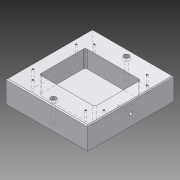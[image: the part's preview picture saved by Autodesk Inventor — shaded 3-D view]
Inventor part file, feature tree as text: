
AUTODESK INVENTOR PART (.ipt)
format: ipt  version: 2013 (Build 170138000, 138)  size: 171,008 bytes
history: native  units: mm
features: sketch x4, hole x3, extrude x2, fillet x1, chamfer x1
ambient origin geometry x8: Origin, YZ Plane, XZ Plane, XY Plane, X Axis, Y Axis, Z Axis, Center Point
bodies: Volumenkörper1 (feature_tree)
feature tree (11):
  extrude  "Extrusion1"  Depth=180.0mm
  extrude  "Extrusion2"  Depth=116.0mm
  fillet  "Rundung1"  Radius=96.0mm
  chamfer  "Fase1"  Distance=36.0mm
  sketch  "Skizze4"  dims[d10=4.0mm d11=2.0mm d12=2.0mm d13=45.0deg]
  hole  "Bohrung3"  [1 undecoded]
  hole  "Bohrung6"  [1 undecoded]
  hole  "Bohrung7"  [1 undecoded]
  sketch  "Skizze1"  dims[d0=170.0mm d2=180.0mm]
  sketch  "Skizze2"  dims[d3=46.0mm d4=0.0mm d5=116.0mm d7=96.0mm d8=36.0mm d9=0.0mm]
  sketch  "Skizze9"  dims[d14=8.0mm d15=30.0mm d16=30.0mm d17=8.0mm d18=8.0mm d19=30.0mm d20=8.0mm d21=30.0mm d22=30.0mm d23=8.0mm d24=8.0mm d25=30.0mm d26=8.0mm d27=30.0mm d28=30.0mm d29=8.0mm d30=4.0mm d31=4.0mm d32=4.0mm d33=4.0mm d34=4.0mm d35=4.0mm d36=4.0mm d37=4.0mm d92=23.0mm d93=90.0mm d94=4.0mm d95=6.0mm d96=6.0mm d97=10.0mm d98=90.0deg d99=30.0mm d100=20.594885mm d143=152.4mm d145=13.8mm d146=6.756mm d147=6.0mm d148=11.113mm d149=6.35mm d150=14.3117mm d151=50.0mm d152=20.594885mm d153=45.0mm d154=45.0mm d155=11.0mm d156=26.0mm d157=30.0mm d158=11.0mm d159=26.0mm d160=30.0mm d161=30.0mm d162=26.0mm d163=11.0mm d164=45.0mm d165=11.0mm d166=45.0mm d167=26.0mm d168=30.0mm d169=3.242mm d170=6.0mm d171=8.0mm d172=4.6mm d173=14.3117mm d174=20.0mm d175=20.594885mm]
note: 3 required parameter values undecoded (feature->parameter linkage not recoverable at this tier; creation-order binding heuristic only, values carry confidence <= 0.55)
